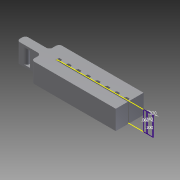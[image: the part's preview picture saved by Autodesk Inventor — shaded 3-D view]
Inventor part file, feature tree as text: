
AUTODESK INVENTOR PART (.ipt)
format: ipt  version: 2013 SP2 (Build 170200200, 200)  size: 271,360 bytes
history: native  units: in
note: dims shown in document units (in); Inventor stores cm internally (conversion verified against a paired STEP export)
features: sketch x10, extrude x9, fillet x3
ambient origin geometry x8: Origin, YZ Plane, XZ Plane, XY Plane, X Axis, Y Axis, Z Axis, Center Point
bodies: Solid1 (feature_tree)
feature tree (22):
  extrude  "Extrusion1"  Depth=0.16in
  extrude  "Extrusion2"  Depth=2.0in
  sketch  "Sketch3"  dims[d33=0.25in d34=0.0in d43=2.0in]
  extrude  "Extrusion4"  Depth=2.0in
  extrude  "Extrusion6"  Depth=0.14in
  extrude  "Extrusion7"  Depth=0.02in
  extrude  "Extrusion8"  Depth=0.14in
  extrude  "Extrusion9"  Depth=0.06in
  extrude  "Extrusion10"  Depth=0.06in
  extrude  "Extrusion11"  Depth=0.06in
  fillet  "Fillet7"  Radius=0.06in
  fillet  "Fillet8"  Radius=0.06in
  fillet  "Fillet9"  Radius=0.06in
  sketch  "Sketch1"  dims[d28=0.4693in d29=0.16in]
  sketch  "Sketch2"  dims[d30=0.4in d31=2.0in]
  sketch  "Sketch5"  dims[d69=0.049in d70=0.0in d71=0.14in]
  sketch  "Sketch9"  dims[d72=0.06in d73=0.02in]
  sketch  "Sketch10"  dims[d74=0.1in d78=0.14in]
  sketch  "Sketch11"  dims[d80=0.06in d82=0.06in]
  sketch  "Sketch12"  dims[d83=0.06in d84=0.06in]
  sketch  "Sketch13"  dims[d85=0.06in d86=0.06in d87=0.06in d88=0.06in d89=0.06in]
  sketch  "Sketch14"  dims[d90=0.06in d91=1.0in d92=0.0in d100=1.5in d102=0.25in d103=0.0in d104=0.25in d105=0.325in d106=0.0in d107=0.25in d108=1.5in d109=0.0in d110=1.5in d111=0.0in d112=0.2in d113=0.2in d114=0.5in d115=0.0in d116=0.2in d117=0.155in d118=0.155in d119=0.075in d120=0.5in d121=0.0in d122=0.0625in d123=0.0625in d124=0.0625in]
